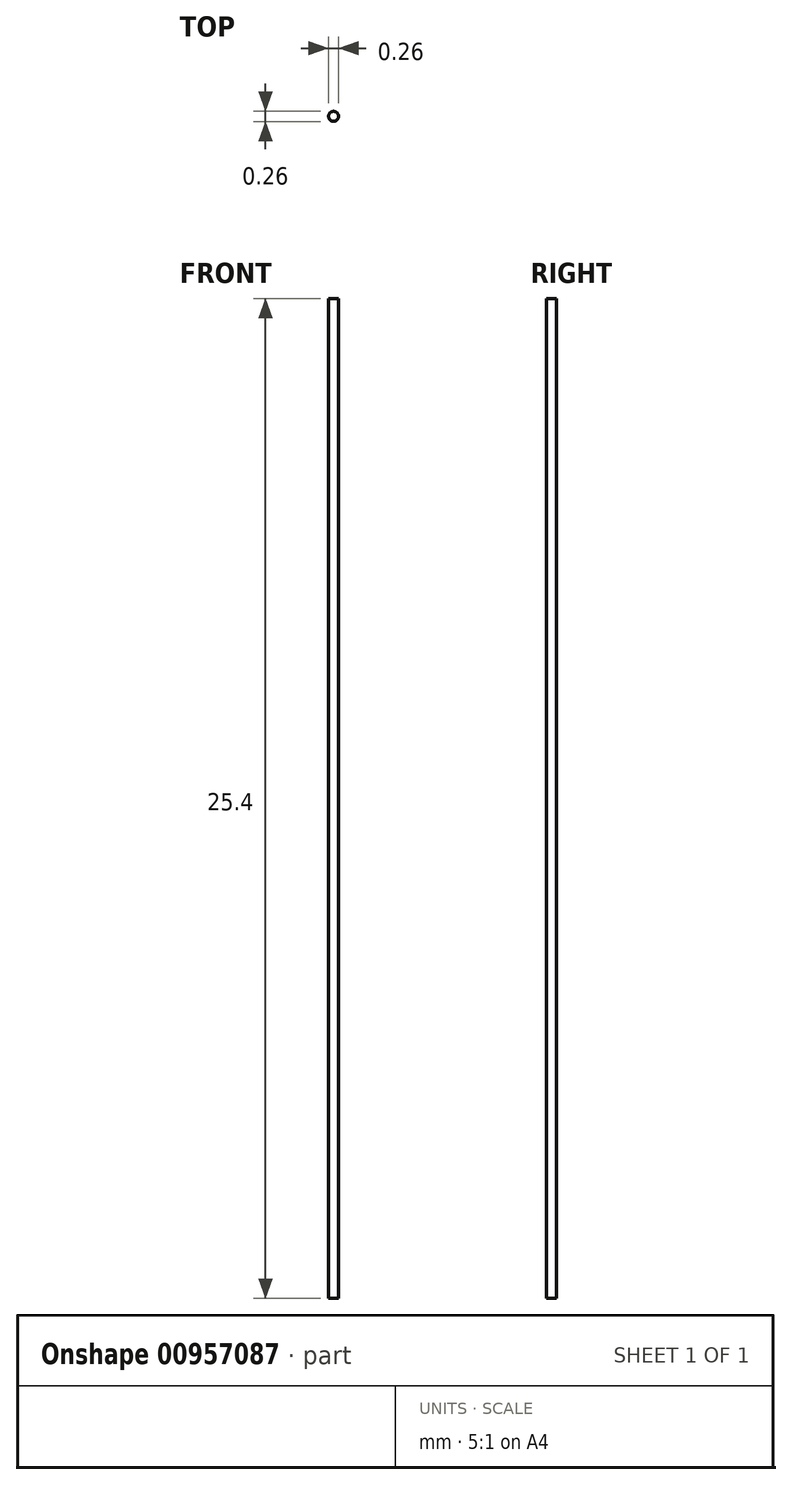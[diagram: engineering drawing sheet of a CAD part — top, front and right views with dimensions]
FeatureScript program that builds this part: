
annotation { "Feature Type Name" : "Feature", "Feature Type Description" : "" }
export const myFeature = defineFeature(function(context is Context, id is Id, definition is map)
    precondition{}
    {
        {
            var Q0;
            Q0=qCreatedBy(makeId("Top.planeOp"),FACE);
            var sketch = newSketch(context, id + "F0", { "sketchPlane" : qUnion([Q0])});
            skCircle(sketch, "E0", {"center": v(0, 0) * mm, "radius": 0.13 * mm});
            skSolve(sketch);
        }
        {
            var Q0;
            Q0=makeQuery(id+"F0.imprint","IMPRINT",FACE,{"disambiguationData":[TD([[makeQuery(id+"F0.imprint","IMPRINT",EDGE,{"derivedFrom":sQuery(id+"F0.wireOp",EDGE,"E0")}),1.0]])]});
            extrude(context, id + "F1", {"entities" : qUnion([Q0]), "depth" : 25.4 * mm, "offsetDistance" : 25.4 * mm});
        }
    });
